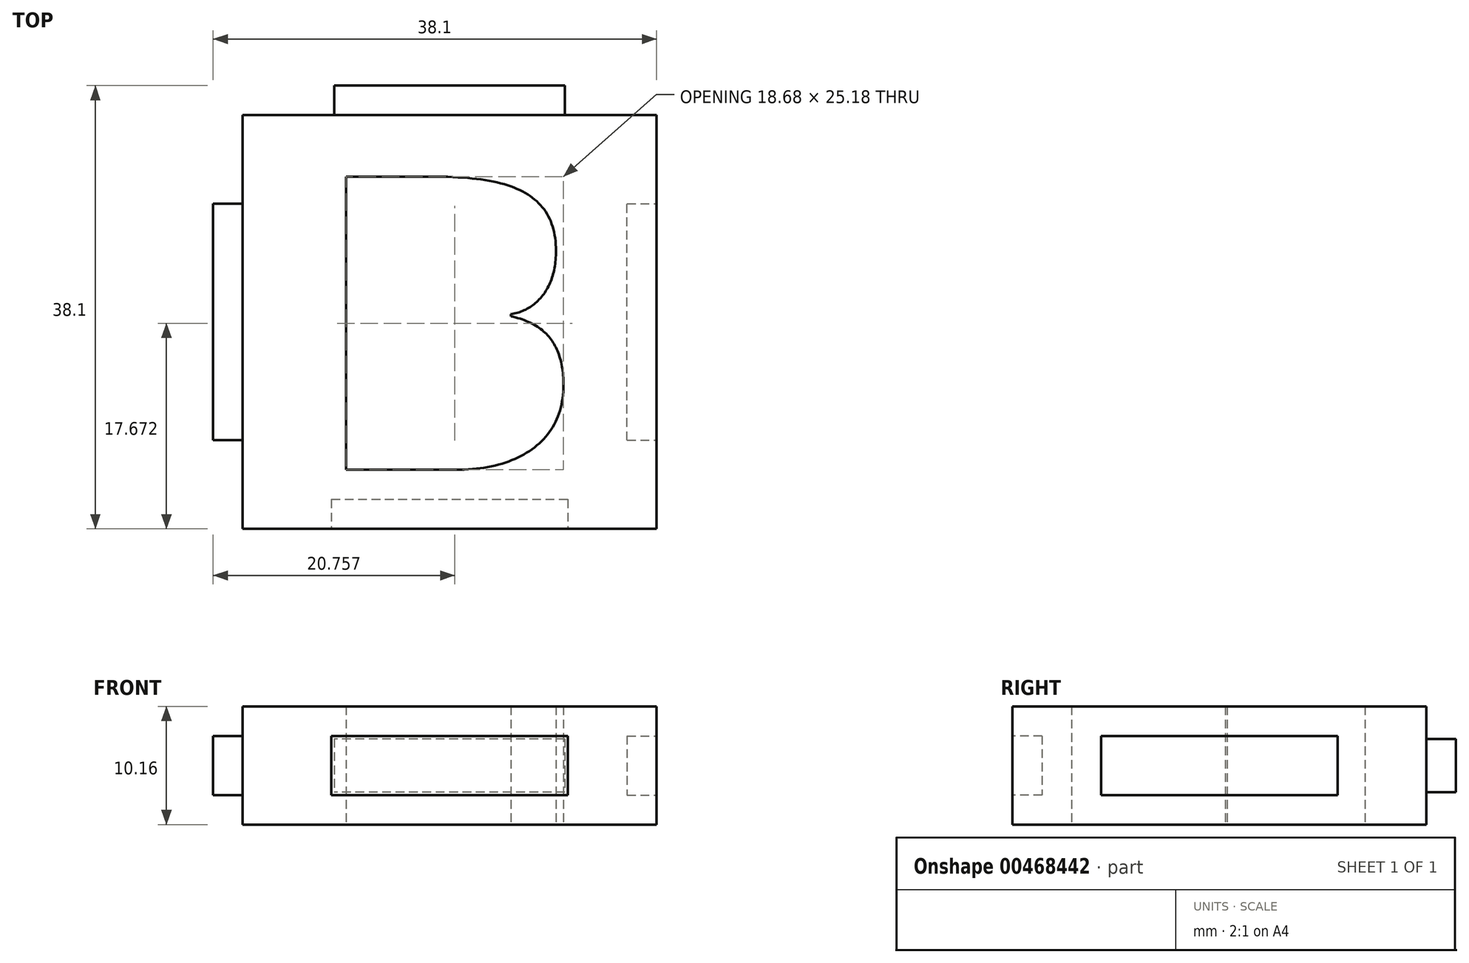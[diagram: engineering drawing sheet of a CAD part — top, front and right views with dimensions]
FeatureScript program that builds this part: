
annotation { "Feature Type Name" : "Feature", "Feature Type Description" : "" }
export const myFeature = defineFeature(function(context is Context, id is Id, definition is map)
    precondition{}
    {
        {
            var Q0;
            Q0=qCreatedBy(makeId("Top.planeOp"),FACE);
            var sketch = newSketch(context, id + "F0", { "sketchPlane" : qUnion([Q0])});
            skLineSegment(sketch, "E0.bottom", {"start": v(-17.78, 17.78) * mm, "end": v(17.78, 17.78) * mm});
            skLineSegment(sketch, "E0.top", {"start": v(-17.78, -17.78) * mm, "end": v(17.78, -17.78) * mm});
            skLineSegment(sketch, "E0.left", {"start": v(-17.78, 17.78) * mm, "end": v(-17.78, -17.78) * mm});
            skLineSegment(sketch, "E0.right", {"start": v(17.78, 17.78) * mm, "end": v(17.78, -17.78) * mm});
            skText(sketch, "E1", { "text": "B", "fontName": "OpenSans-Bold.ttf"});
            const initialGuessF0  = {"E1": [-0.01207, -0.0127, 1, 0, 0.0254]};
            skSetInitialGuess(sketch, initialGuessF0);
            skSolve(sketch);
        }
        {
            var Q0;
            Q0=qSketchRegion(id+"F0",true);
            extrude(context, id + "F1", {"entities" : qUnion([Q0]), "endBound" : BoundingType.SYMMETRIC, "depth" : 10.16 * mm});
        }
        {
            var Q0;
            Q0=makeQuery(id+"F1.opExtrude","SWEPT_FACE",FACE,{"disambiguationData":[OSD([sQuery(id+"F0.wireOp",EDGE,"E0.bottom")])]});
            var sketch = newSketch(context, id + "F2", { "sketchPlane" : qUnion([Q0])});
            skLineSegment(sketch, "E2.bottom", {"start": v(-9.9, 2.29) * mm, "end": v(9.9, 2.29) * mm});
            skLineSegment(sketch, "E2.top", {"start": v(-9.9, -2.29) * mm, "end": v(9.9, -2.29) * mm});
            skLineSegment(sketch, "E2.left", {"start": v(-9.9, 2.29) * mm, "end": v(-9.9, -2.29) * mm});
            skLineSegment(sketch, "E2.right", {"start": v(9.9, 2.29) * mm, "end": v(9.9, -2.29) * mm});
            skSolve(sketch);
        }
        {
            var Q0;
            Q0=qSketchRegion(id+"F2",true);
            extrude(context, id + "F3", {"entities" : qUnion([Q0]), "operationType" : NewBodyOperationType.ADD, "depth" : 2.54 * mm});
        }
        {
            var Q0;
            Q0=makeQuery(id+"F1.opExtrude","SWEPT_FACE",FACE,{"disambiguationData":[OSD([sQuery(id+"F0.wireOp",EDGE,"E0.left")])]});
            var sketch = newSketch(context, id + "F4", { "sketchPlane" : qUnion([Q0])});
            skLineSegment(sketch, "E3.bottom", {"start": v(-10.16, 2.54) * mm, "end": v(10.16, 2.54) * mm});
            skLineSegment(sketch, "E3.top", {"start": v(-10.16, -2.54) * mm, "end": v(10.16, -2.54) * mm});
            skLineSegment(sketch, "E3.left", {"start": v(-10.16, 2.54) * mm, "end": v(-10.16, -2.54) * mm});
            skLineSegment(sketch, "E3.right", {"start": v(10.16, 2.54) * mm, "end": v(10.16, -2.54) * mm});
            skSolve(sketch);
        }
        {
            var Q0;
            Q0=qSketchRegion(id+"F4",true);
            extrude(context, id + "F5", {"entities" : qUnion([Q0]), "operationType" : NewBodyOperationType.ADD, "depth" : 2.54 * mm});
        }
        {
            var Q0;
            Q0=makeQuery(id+"F1.opExtrude","SWEPT_FACE",FACE,{"disambiguationData":[OSD([sQuery(id+"F0.wireOp",EDGE,"E0.top")])]});
            var sketch = newSketch(context, id + "F6", { "sketchPlane" : qUnion([Q0])});
            skLineSegment(sketch, "E4.bottom", {"start": v(-10.16, 2.54) * mm, "end": v(10.16, 2.54) * mm});
            skLineSegment(sketch, "E4.top", {"start": v(-10.16, -2.54) * mm, "end": v(10.16, -2.54) * mm});
            skLineSegment(sketch, "E4.left", {"start": v(-10.16, 2.54) * mm, "end": v(-10.16, -2.54) * mm});
            skLineSegment(sketch, "E4.right", {"start": v(10.16, 2.54) * mm, "end": v(10.16, -2.54) * mm});
            skSolve(sketch);
        }
        {
            var Q0;
            Q0=qSketchRegion(id+"F6",true);
            extrude(context, id + "F7", {"entities" : qUnion([Q0]), "operationType" : NewBodyOperationType.REMOVE, "oppositeDirection" : true, "depth" : 2.54 * mm});
        }
        {
            var Q0;
            Q0=makeQuery(id+"F1.opExtrude","SWEPT_FACE",FACE,{"disambiguationData":[OSD([sQuery(id+"F0.wireOp",EDGE,"E0.right")])]});
            var sketch = newSketch(context, id + "F8", { "sketchPlane" : qUnion([Q0])});
            skLineSegment(sketch, "E5.bottom", {"start": v(-10.16, 2.54) * mm, "end": v(10.16, 2.54) * mm});
            skLineSegment(sketch, "E5.top", {"start": v(-10.16, -2.54) * mm, "end": v(10.16, -2.54) * mm});
            skLineSegment(sketch, "E5.left", {"start": v(-10.16, 2.54) * mm, "end": v(-10.16, -2.54) * mm});
            skLineSegment(sketch, "E5.right", {"start": v(10.16, 2.54) * mm, "end": v(10.16, -2.54) * mm});
            skSolve(sketch);
        }
        {
            var Q0;
            Q0=qSketchRegion(id+"F8",true);
            extrude(context, id + "F9", {"entities" : qUnion([Q0]), "operationType" : NewBodyOperationType.REMOVE, "oppositeDirection" : true, "depth" : 2.54 * mm});
        }
    });
